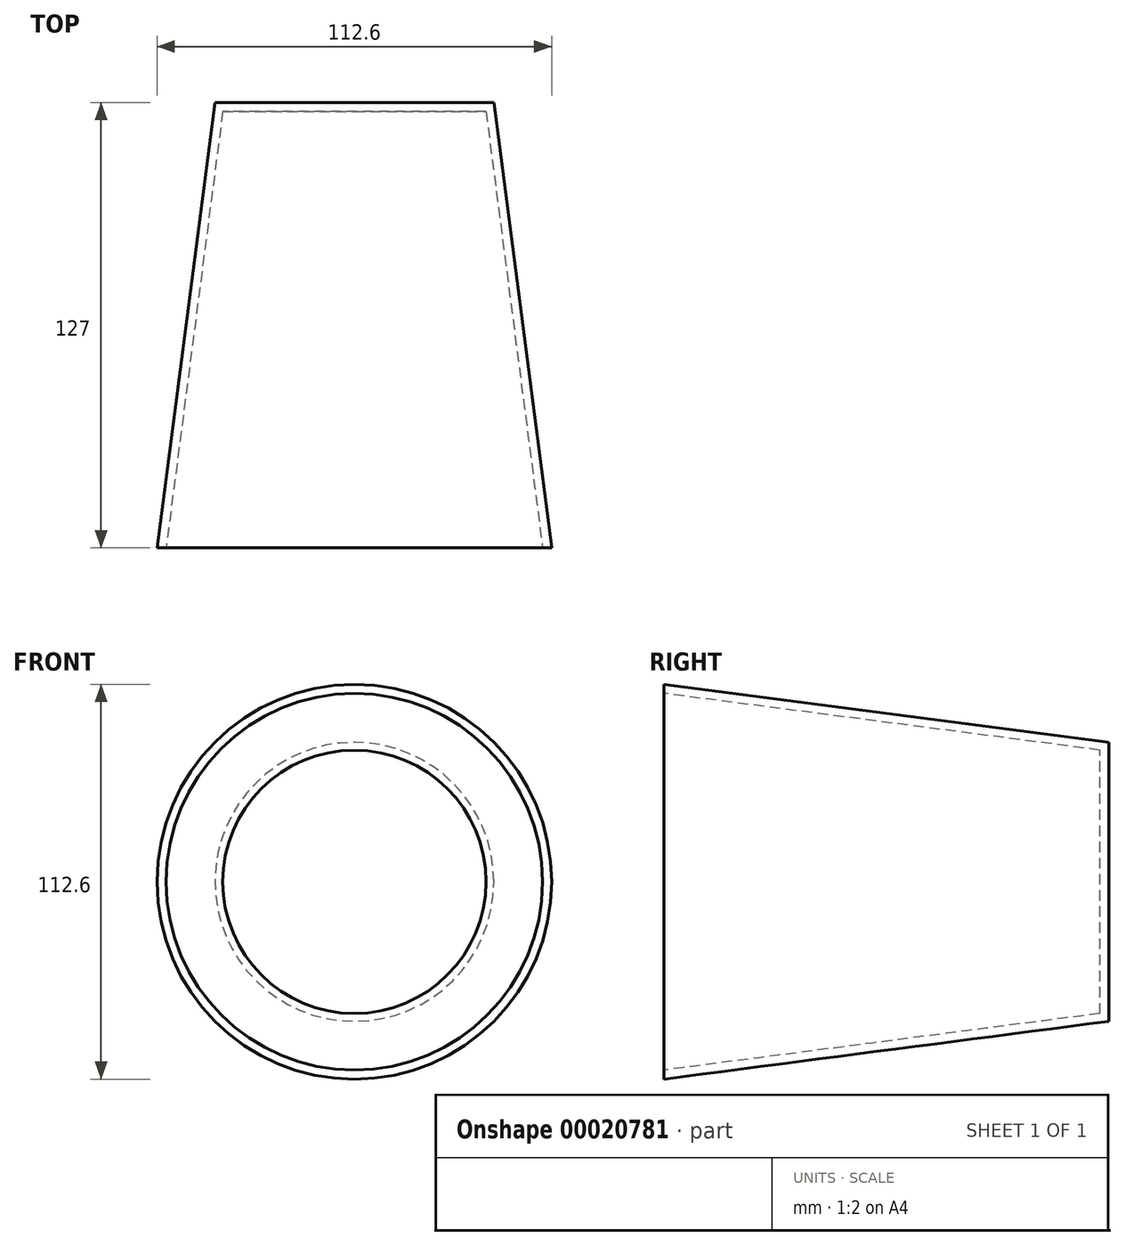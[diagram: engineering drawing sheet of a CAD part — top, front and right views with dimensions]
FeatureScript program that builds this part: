
annotation { "Feature Type Name" : "Feature", "Feature Type Description" : "" }
export const myFeature = defineFeature(function(context is Context, id is Id, definition is map)
    precondition{}
    {
        {
            var Q0;
            Q0=qCreatedBy(makeId("Front.planeOp"),FACE);
            cPlane(context, id + "F0", {"entities" : qUnion([Q0]), "cplaneType" : CPlaneType.OFFSET, "offset" : 127 * mm, "width" : 152.4 * mm, "height" : 152.4 * mm});
        }
        {
            var Q0;
            Q0=qCreatedBy(makeId("Front.planeOp"),FACE);
            var sketch = newSketch(context, id + "F1", { "sketchPlane" : qUnion([Q0])});
            skCircle(sketch, "E0", {"center": v(0, 0) * mm, "radius": 39.8 * mm});
            skSolve(sketch);
        }
        {
            var Q0;
            Q0=qCreatedBy(id+"F0.planeOp",FACE);
            var sketch = newSketch(context, id + "F2", { "sketchPlane" : qUnion([Q0])});
            skCircle(sketch, "E1", {"center": v(0, 0) * mm, "radius": 56.3 * mm});
            skSolve(sketch);
        }
        {
            var Q0;
            Q0=makeQuery(id+"F2.imprint","IMPRINT",FACE,{"disambiguationData":[TD([[makeQuery(id+"F2.imprint","IMPRINT",EDGE,{"derivedFrom":sQuery(id+"F2.wireOp",EDGE,"E1")}),1.0]])]});
            var Q1;
            Q1=makeQuery(id+"F1.imprint","IMPRINT",FACE,{"disambiguationData":[TD([[makeQuery(id+"F1.imprint","IMPRINT",EDGE,{"derivedFrom":sQuery(id+"F1.wireOp",EDGE,"E0")}),1.0]])]});
            loft(context, id + "F3", {"sheetProfilesArray" : [{ "sheetProfileEntities" : qUnion([Q0]) }, { "sheetProfileEntities" : qUnion([Q1]) }]});
        }
        {
            var Q0;
            Q0=makeQuery(id+"F3.opLoft","CAP_FACE",FACE,{"disambiguationData":[OSD([makeQuery(id+"F2.imprint","IMPRINT",FACE,{"disambiguationData":[TD([[makeQuery(id+"F2.imprint","IMPRINT",EDGE,{"derivedFrom":sQuery(id+"F2.wireOp",EDGE,"E1")}),1.0]])]})])],"isStart":true});
            shell(context, id + "F4", {"entities" : qUnion([Q0]), "thickness" : 2.54 * mm});
        }
    });
